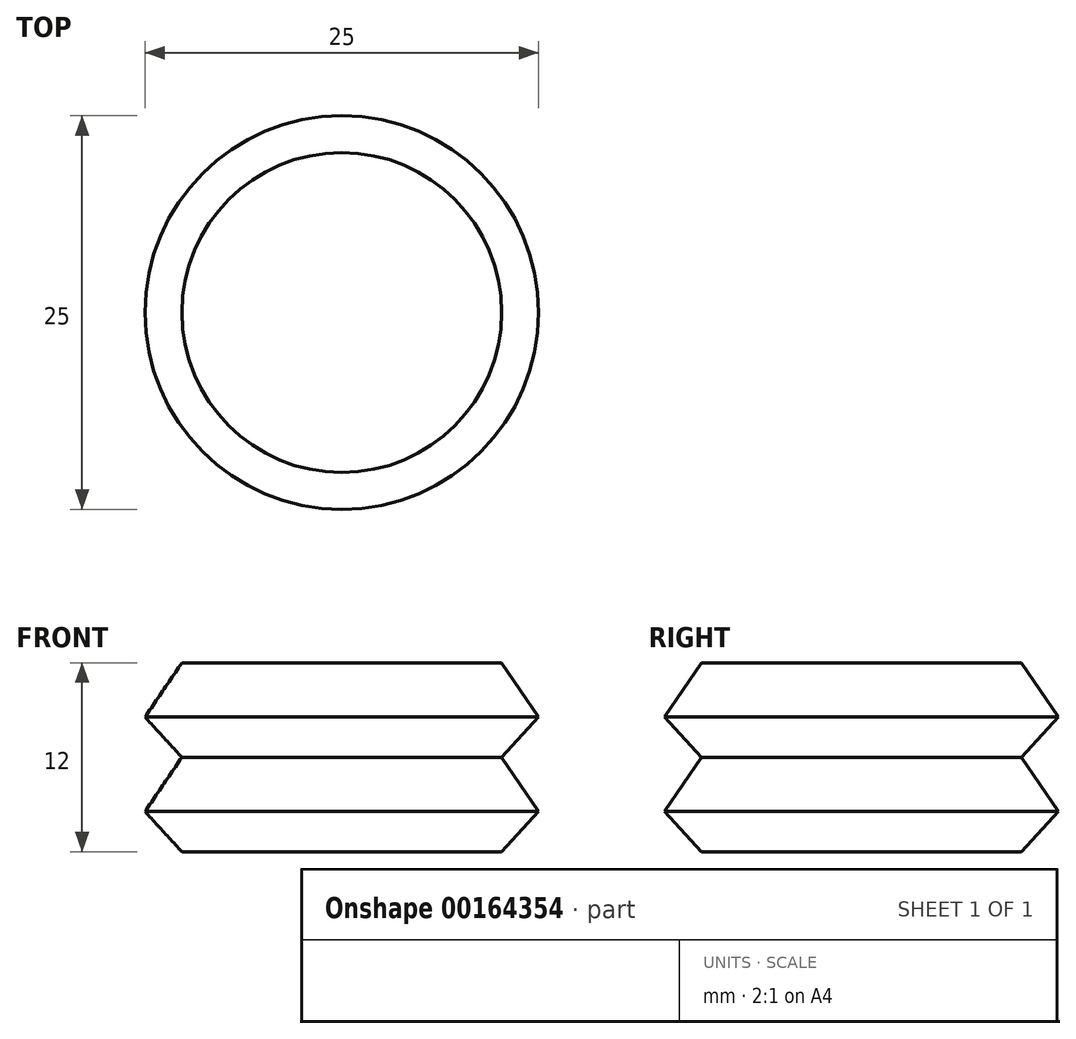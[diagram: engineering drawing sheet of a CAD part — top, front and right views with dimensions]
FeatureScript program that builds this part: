
annotation { "Feature Type Name" : "Feature", "Feature Type Description" : "" }
export const myFeature = defineFeature(function(context is Context, id is Id, definition is map)
    precondition{}
    {
        {
            var Q0;
            Q0=qCreatedBy(makeId("Front.planeOp"),FACE);
            var sketch = newSketch(context, id + "F0", { "sketchPlane" : qUnion([Q0])});
            skLineSegment(sketch, "E0", {"start": v(0, 32.82) * mm, "end": v(10.16, 32.82) * mm});
            skLineSegment(sketch, "E1", {"start": v(10.16, 32.82) * mm, "end": v(12.5, 29.37) * mm});
            skLineSegment(sketch, "E2", {"start": v(12.5, 29.37) * mm, "end": v(10.16, 26.82) * mm});
            skLineSegment(sketch, "E3", {"start": v(10.16, 26.82) * mm, "end": v(12.5, 23.37) * mm});
            skLineSegment(sketch, "E4", {"start": v(12.5, 23.37) * mm, "end": v(10.16, 20.82) * mm});
            skLineSegment(sketch, "E5", {"start": v(10.16, 20.82) * mm, "end": v(0, 20.82) * mm});
            skLineSegment(sketch, "E6", {"start": v(0, 20.82) * mm, "end": v(0, 32.82) * mm});
            skSolve(sketch);
        }
        {
            var Q0;
            Q0 = qSketchRegion(id + "F0", true);
            var Q1;
            Q1=sQuery(id+"F0.wireOp",EDGE,"E6");
            revolve(context, id + "F1", {"entities" : qUnion([Q0]), "axis" : qUnion([Q1]), "revolveType" : RevolveType.FULL});
        }
    });
